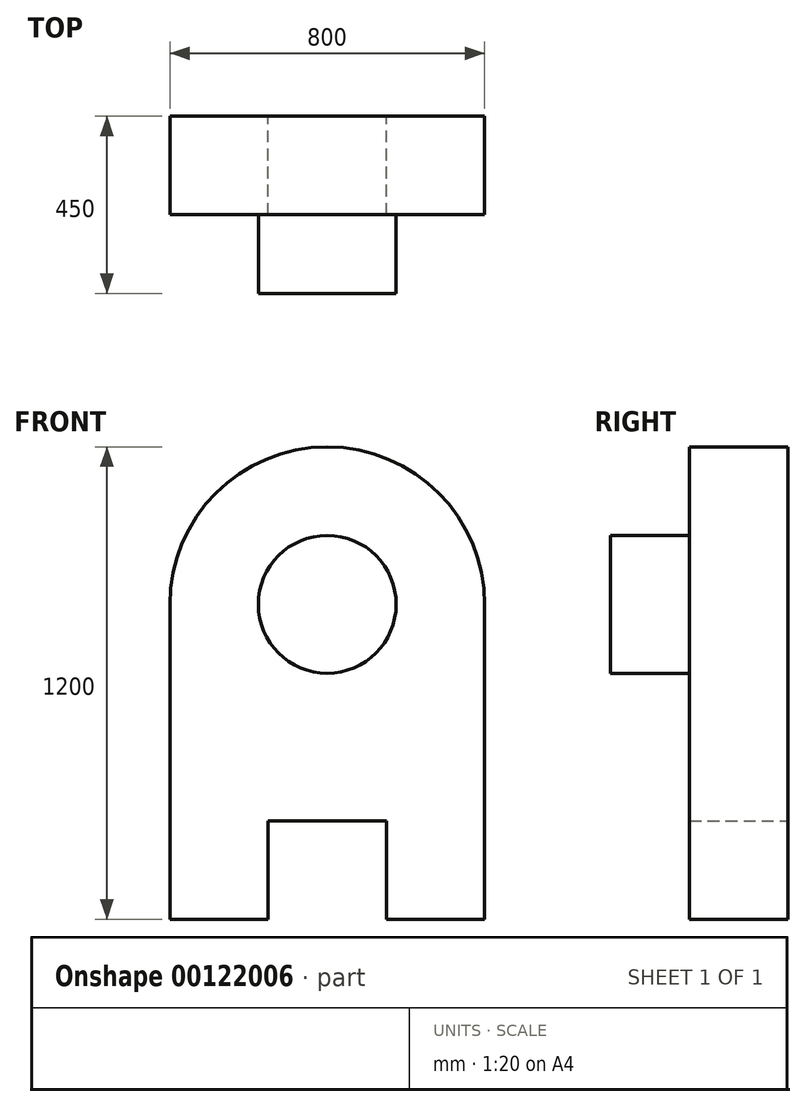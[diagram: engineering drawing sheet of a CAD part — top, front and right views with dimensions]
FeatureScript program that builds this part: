
annotation { "Feature Type Name" : "Feature", "Feature Type Description" : "" }
export const myFeature = defineFeature(function(context is Context, id is Id, definition is map)
    precondition{}
    {
        {
            var Q0;
            Q0=qCreatedBy(makeId("Front.planeOp"),FACE);
            var sketch = newSketch(context, id + "F0", { "sketchPlane" : qUnion([Q0])});
            skLineSegment(sketch, "E0.bottom", {"start": v(-400, -400) * mm, "end": v(-150, -400) * mm});
            skLineSegment(sketch, "E0.left", {"start": v(-400, -400) * mm, "end": v(-400, 400) * mm});
            skLineSegment(sketch, "E0.right", {"start": v(400, -400) * mm, "end": v(400, 400) * mm});
            skPoint(sketch, "E0.middle", {"position": v(0, 0) * mm});
            skArc(sketch, "E1", {"start": v(400, 400) * mm, "mid": v(0, 800) * mm, "end": v(-400, 400) * mm});
            skLineSegment(sketch, "E2.top", {"start": v(-150, -150) * mm, "end": v(150, -150) * mm});
            skLineSegment(sketch, "E2.left", {"start": v(-150, -400) * mm, "end": v(-150, -150) * mm});
            skLineSegment(sketch, "E2.right", {"start": v(150, -400) * mm, "end": v(150, -150) * mm});
            skPoint(sketch, "E2.middle", {"position": v(0, -400) * mm});
            skPoint(sketch, "E2.bottom.end.orphan", {"position": v(150, -650) * mm});
            skPoint(sketch, "E2.bottom.start.orphan", {"position": v(-150, -650) * mm});
            skLineSegment(sketch, "E3.trimOffspring", {"start": v(150, -400) * mm, "end": v(400, -400) * mm});
            skSolve(sketch);
        }
        {
            var Q0;
            Q0 = qSketchRegion(id + "F0", true);
            extrude(context, id + "F1", {"entities" : qUnion([Q0]), "depth" : 250 * mm});
        }
        {
            var Q0;
            Q0=makeQuery(id+"F1.opExtrude","CAP_FACE",FACE,{"disambiguationData":[OSD([sQuery(id+"F0.wireOp",EDGE,"E0.bottom"),sQuery(id+"F0.wireOp",EDGE,"E0.left"),sQuery(id+"F0.wireOp",EDGE,"E0.right"),sQuery(id+"F0.wireOp",EDGE,"E1"),sQuery(id+"F0.wireOp",EDGE,"E2.top"),sQuery(id+"F0.wireOp",EDGE,"E2.left"),sQuery(id+"F0.wireOp",EDGE,"E2.right"),sQuery(id+"F0.wireOp",EDGE,"E3.trimOffspring")])],"isStart":false});
            var sketch = newSketch(context, id + "F2", { "sketchPlane" : qUnion([Q0])});
            skCircle(sketch, "E4", {"center": v(0, 400) * mm, "radius": 175 * mm});
            skSolve(sketch);
        }
        {
            var Q0;
            Q0 = qSketchRegion(id + "F2", true);
            extrude(context, id + "F3", {"entities" : qUnion([Q0]), "operationType" : NewBodyOperationType.ADD, "depth" : 200 * mm});
        }
    });
